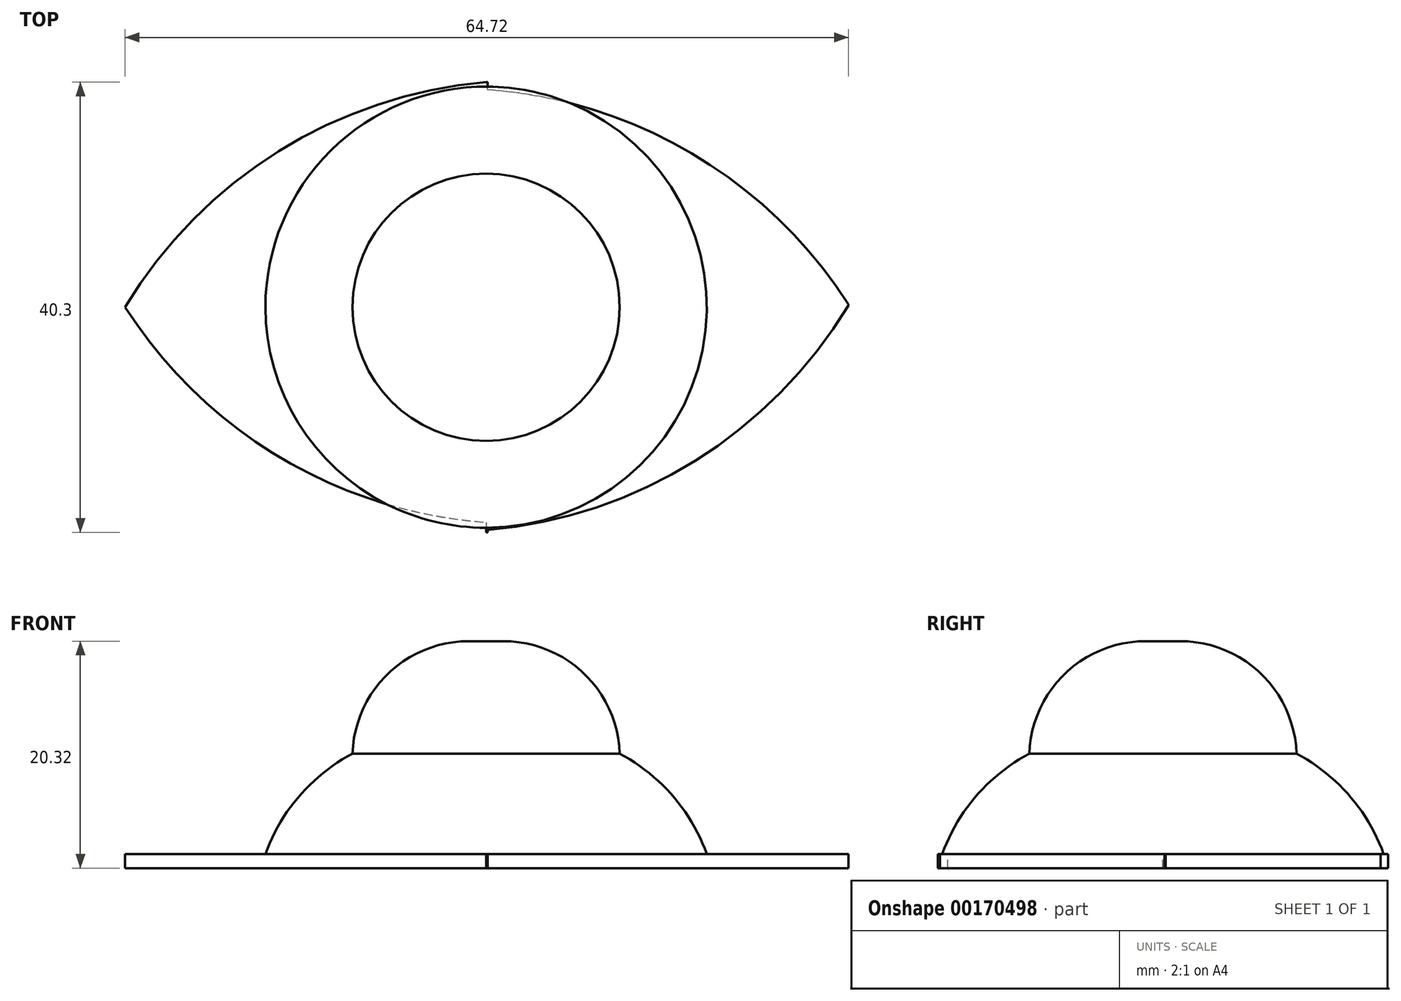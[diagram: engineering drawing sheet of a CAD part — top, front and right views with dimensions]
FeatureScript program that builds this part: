
annotation { "Feature Type Name" : "Feature", "Feature Type Description" : "" }
export const myFeature = defineFeature(function(context is Context, id is Id, definition is map)
    precondition{}
    {
        {
            var Q0;
            Q0=qCreatedBy(makeId("Top.planeOp"),FACE);
            var sketch = newSketch(context, id + "F0", { "sketchPlane" : qUnion([Q0])});
            skCircle(sketch, "E0", {"center": v(0, 0) * mm, "radius": 19.75 * mm});
            skSolve(sketch);
        }
        {
            var Q0;
            Q0=makeQuery(id+"F0.imprint","IMPRINT",FACE,{"disambiguationData":[TD([[makeQuery(id+"F0.imprint","IMPRINT",EDGE,{"derivedFrom":sQuery(id+"F0.wireOp",EDGE,"E0")}),1.0]])]});
            extrude(context, id + "F1", {"entities" : qUnion([Q0]), "depth" : 10.92 * mm});
        }
        {
            var Q0;
            Q0=makeQuery(id+"F1.opExtrude","CAP_FACE",FACE,{"disambiguationData":[OSD([sQuery(id+"F0.wireOp",EDGE,"E0")])],"isStart":false});
            fillet(context, id + "F2", {"entities" : qUnion([Q0]), "radius" : 16.56 * mm, "tangentPropagation" : true, "allowEdgeOverflow" : false});
        }
        {
            var Q0;
            Q0=qCreatedBy(makeId("Top.planeOp"),FACE);
            var sketch = newSketch(context, id + "F3", { "sketchPlane" : qUnion([Q0])});
            skLineSegment(sketch, "E1.bottom", {"start": v(32.42, 20.15) * mm, "end": v(-32.42, 20.15) * mm});
            skLineSegment(sketch, "E1.top", {"start": v(32.42, -20.15) * mm, "end": v(-32.42, -20.15) * mm});
            skLineSegment(sketch, "E1.left", {"start": v(32.42, 20.15) * mm, "end": v(32.42, -20.15) * mm});
            skLineSegment(sketch, "E1.right", {"start": v(-32.42, 20.15) * mm, "end": v(-32.42, -20.15) * mm});
            skPoint(sketch, "E1.middle", {"position": v(0, 0) * mm});
            skSolve(sketch);
        }
        {
            var Q0;
            Q0=makeQuery(id+"F3.imprint","IMPRINT",FACE,{"disambiguationData":[TD([[makeQuery(id+"F3.imprint","IMPRINT",EDGE,{"derivedFrom":sQuery(id+"F3.wireOp",EDGE,"E1.bottom")}),1.0]])]});
            extrude(context, id + "F4", {"entities" : qUnion([Q0]), "operationType" : NewBodyOperationType.ADD, "oppositeDirection" : true, "depth" : 1.27 * mm});
        }
        {
            var Q0;
            Q0=qCreatedBy(makeId("Top.planeOp"),FACE);
            var sketch = newSketch(context, id + "F5", { "sketchPlane" : qUnion([Q0])});
            skArc(sketch, "E2", {"start": v(-32.3, 0) * mm, "mid": v(-18.43, -13.46) * mm, "end": v(0, -19.26) * mm});
            skArc(sketch, "E3", {"start": v(0, 20.15) * mm, "mid": v(-18.57, 13.95) * mm, "end": v(-32.3, 0) * mm});
            skLineSegment(sketch, "E4", {"start": v(0, -19.26) * mm, "end": v(0, -56) * mm});
            skLineSegment(sketch, "E5", {"start": v(0, -56) * mm, "end": v(-63.71, -56) * mm});
            skLineSegment(sketch, "E6", {"start": v(-63.71, -56) * mm, "end": v(-63.71, 55.41) * mm});
            skLineSegment(sketch, "E7", {"start": v(-63.71, 55.41) * mm, "end": v(0, 55.41) * mm});
            skLineSegment(sketch, "E8", {"start": v(0, 55.41) * mm, "end": v(0, 20.15) * mm});
            skSolve(sketch);
        }
        {
            var Q0;
            Q0=qCreatedBy(makeId("Top.planeOp"),FACE);
            var sketch = newSketch(context, id + "F6", { "sketchPlane" : qUnion([Q0])});
            skArc(sketch, "E9", {"start": v(32.45, 0.2) * mm, "mid": v(18.58, 13.66) * mm, "end": v(0.15, 19.47) * mm});
            skArc(sketch, "E10", {"start": v(0.15, -19.94) * mm, "mid": v(18.72, -13.75) * mm, "end": v(32.45, 0.2) * mm});
            skLineSegment(sketch, "E11", {"start": v(0.15, 19.47) * mm, "end": v(0.15, 56.21) * mm});
            skLineSegment(sketch, "E12", {"start": v(0.15, 56.21) * mm, "end": v(63.86, 56.21) * mm});
            skLineSegment(sketch, "E13", {"start": v(63.86, 56.21) * mm, "end": v(63.86, -54.91) * mm});
            skLineSegment(sketch, "E14", {"start": v(63.86, -54.91) * mm, "end": v(0.15, -54.91) * mm});
            skLineSegment(sketch, "E15", {"start": v(0.15, -54.91) * mm, "end": v(0.15, -19.94) * mm});
            skSolve(sketch);
        }
        {
            var Q0;
            Q0=makeQuery(id+"F6.imprint","IMPRINT",FACE,{"disambiguationData":[TD([[makeQuery(id+"F6.imprint","IMPRINT",EDGE,{"derivedFrom":sQuery(id+"F6.wireOp",EDGE,"E9")}),-1.0]])]});
            extrude(context, id + "F7", {"entities" : qUnion([Q0]), "operationType" : NewBodyOperationType.REMOVE, "oppositeDirection" : true, "depth" : 128.78 * mm});
        }
        {
            var Q0;
            Q0=makeQuery(id+"F5.imprint","IMPRINT",FACE,{"disambiguationData":[TD([[makeQuery(id+"F5.imprint","IMPRINT",EDGE,{"derivedFrom":sQuery(id+"F5.wireOp",EDGE,"E2")}),-1.0]])]});
            extrude(context, id + "F8", {"entities" : qUnion([Q0]), "operationType" : NewBodyOperationType.REMOVE, "oppositeDirection" : true, "depth" : 25.4 * mm});
        }
        {
            var Q0;
            Q0=qCreatedBy(makeId("Top.planeOp"),FACE);
            var sketch = newSketch(context, id + "F9", { "sketchPlane" : qUnion([Q0])});
            skCircle(sketch, "E16", {"center": v(0, 0) * mm, "radius": 11.96 * mm});
            skSolve(sketch);
        }
        {
            var Q0;
            Q0 = qSketchRegion(id + "F9", true);
            extrude(context, id + "F10", {"entities" : qUnion([Q0]), "operationType" : NewBodyOperationType.ADD, "depth" : 19.05 * mm});
        }
        {
            var Q0;
            Q0=makeQuery(id+"F10.opExtrude","CAP_FACE",FACE,{"disambiguationData":[OSD([sQuery(id+"F9.wireOp",EDGE,"E16")])],"isStart":false});
            fillet(context, id + "F11", {"entities" : qUnion([Q0]), "radius" : 10.42 * mm, "tangentPropagation" : true, "allowEdgeOverflow" : false});
        }
    });
